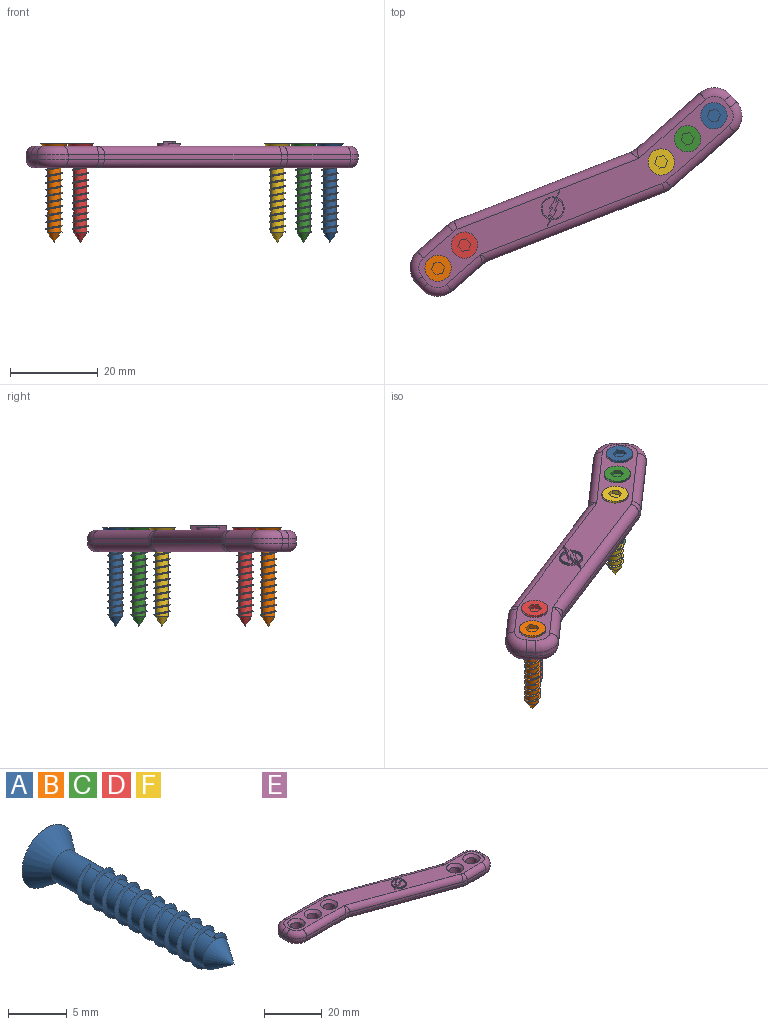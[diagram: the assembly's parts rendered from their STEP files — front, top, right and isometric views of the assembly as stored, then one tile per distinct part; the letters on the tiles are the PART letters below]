
ASSEMBLY  parts=6 mates=5
PART A: 25 faces, bbox 6x22.5x6 mm
  f0: plane 6x6mm, normal (0,1,0), area 22.4mm2, adj f12,f18,f19,f20,f21,f22,f23
  f1: cylinder r=1.5mm len=4.5mm, axis (0,1,0), area 35.3mm2, adj f10,f12,f13,f16
  f2: cylinder r=1.5mm len=3mm, axis (0,1,0), area 11.3mm2, adj f3,f11,f15,f16
  f3: cylinder r=1.5mm len=3mm, axis (0,1,0), area 11.3mm2, adj f2,f4,f15,f16
  f4: cylinder r=1.5mm len=3mm, axis (0,1,0), area 11.3mm2, adj f3,f5,f15,f16
  f5: cylinder r=1.5mm len=3mm, axis (0,1,0), area 11.3mm2, adj f4,f6,f15,f16
  f6: cylinder r=1.5mm len=3mm, axis (0,1,0), area 11.3mm2, adj f5,f7,f15,f16
  f7: cylinder r=1.5mm len=3mm, axis (0,1,0), area 11.3mm2, adj f6,f8,f15,f16
  f8: cylinder r=1.5mm len=3mm, axis (0,1,0), area 11.3mm2, adj f7,f9,f15,f16
  f9: cylinder r=1.5mm len=3mm, axis (0,1,0), area 11.3mm2, adj f8,f10,f15,f16
  f10: cylinder r=1.5mm len=3mm, axis (0,1,0), area 11.3mm2, adj f1,f9,f15,f16
  f11: cylinder r=1.5mm len=3mm, axis (0,1,0), area 7.1mm2, adj f2,f14,f15,f17
  f12: cone r=3mm half-angle=36.9deg, axis (0,1,0), area 35.3mm2, adj f0,f1
  f13: plane 0.37x0.3mm, normal (1,0,0), area 0.1mm2, adj f1,f15,f16
  f14: plane 0.37x0.3mm, normal (-1,0,0), area 0.1mm2, adj f11,f15,f16
  f15: bspline ~15.15x4.32mm, area 42.6mm2, adj f2,f3,f4,f5,f6,f7,f8,f9
  f16: bspline ~15.15x4.32mm, area 42.7mm2, adj f1,f2,f3,f4,f5,f6,f7,f8
  f17: cone r=1.5mm half-angle=34.3deg, axis (0,1,0), area 12.5mm2, adj f11
  f18: plane 1.3x1mm, normal (-0.5,0,-0.87), area 1.5mm2, adj f0,f19,f23,f24
  f19: plane 1.5x1mm, normal (-1,0,0), area 1.5mm2, adj f0,f18,f20,f24
  f20: plane 1.3x1mm, normal (-0.5,0,0.87), area 1.5mm2, adj f0,f19,f21,f24
  f21: plane 1.3x1mm, normal (0.5,0,0.87), area 1.5mm2, adj f0,f20,f22,f24
  f22: plane 1.5x1mm, normal (1,0,0), area 1.5mm2, adj f0,f21,f23,f24
  f23: plane 1.3x1mm, normal (0.5,0,-0.87), area 1.5mm2, adj f0,f18,f22,f24
  f24: plane 3x2.6mm, normal (0,1,0), area 5.8mm2, adj f18,f19,f20,f21,f22,f23
PART B: same geometry as A
PART C: same geometry as A
PART D: same geometry as A
PART E: 81 faces, bbox 83.1x28.2x6 mm
  f0: plane 78.29x23.39mm, normal (0,0,1), area 458.3mm2, adj f23,f24,f25,f26,f27,f28,f29,f30
  f1: plane 78.29x23.39mm, normal (0,0,-1), area 544.8mm2, adj f10,f11,f12,f13,f14,f15,f16,f17
  f2: plane 2x1mm, normal (-1,0,0), area 2mm2, adj f16,f24,f44,f47
  f3: plane 19.12x1mm, normal (0,-1,0), area 19.1mm2, adj f18,f26,f47,f50
  f4: plane 40.63x14.79mm, normal (-0.34,-0.94,0), area 43.2mm2, adj f20,f28,f35,f50
  f5: plane 9.12x1mm, normal (0,-1,0), area 9.1mm2, adj f22,f30,f32,f35
  f6: plane 2x1mm, normal (1,0,0), area 2mm2, adj f21,f29,f32,f38
  f7: plane 9.12x1mm, normal (0,1,0), area 9.1mm2, adj f19,f27,f38,f53
  f8: plane 40.63x14.79mm, normal (0.34,0.94,0), area 43.2mm2, adj f17,f25,f41,f53
  f9: plane 19.12x1mm, normal (0,1,0), area 19.1mm2, adj f15,f23,f41,f44
  f10: cylinder r=2mm len=4mm, axis (0,0,1), area 50.3mm2, adj f1,f56
  f11: cylinder r=2mm len=4mm, axis (0,0,1), area 50.3mm2, adj f1,f59
  f12: cylinder r=2mm len=4mm, axis (0,0,1), area 50.3mm2, adj f1,f57
  f13: cylinder r=2mm len=4mm, axis (0,0,1), area 50.3mm2, adj f1,f58
  f14: cylinder r=2mm len=4mm, axis (0,0,1), area 50.3mm2, adj f1,f55
  f15: cylinder r=2mm len=19.12mm, axis (-1,0,0), area 60.1mm2, adj f1,f9,f42,f45
  f16: cylinder r=2mm len=2mm, axis (0,-1,0), area 6.3mm2, adj f1,f2,f45,f48
  f17: cylinder r=2mm len=42.47mm, axis (-0.94,0.34,0), area 137.2mm2, adj f1,f8,f42,f52
  f18: cylinder r=2mm len=20.35mm, axis (1,0,0), area 61.5mm2, adj f1,f3,f48,f49
  f19: cylinder r=2mm len=10.35mm, axis (-1,0,0), area 30.1mm2, adj f1,f7,f39,f52
  f20: cylinder r=2mm len=42.47mm, axis (0.94,-0.34,0), area 137.2mm2, adj f1,f4,f36,f49
  f21: cylinder r=2mm len=2mm, axis (0,1,0), area 6.3mm2, adj f1,f6,f33,f39
  f22: cylinder r=2mm len=9.12mm, axis (1,0,0), area 28.6mm2, adj f1,f5,f33,f36
  f23: cylinder r=2mm len=19.12mm, axis (1,0,0), area 60.1mm2, adj f0,f9,f40,f43
  f24: cylinder r=2mm len=2mm, axis (0,1,0), area 6.3mm2, adj f0,f2,f43,f46
  f25: cylinder r=2mm len=42.47mm, axis (0.94,-0.34,0), area 137.2mm2, adj f0,f8,f40,f54
  f26: cylinder r=2mm len=20.35mm, axis (-1,0,0), area 61.5mm2, adj f0,f3,f46,f51
  f27: cylinder r=2mm len=10.35mm, axis (1,0,0), area 30.1mm2, adj f0,f7,f37,f54
  f28: cylinder r=2mm len=42.47mm, axis (-0.94,0.34,0), area 137.2mm2, adj f0,f4,f34,f51
  f29: cylinder r=2mm len=2mm, axis (0,-1,0), area 6.3mm2, adj f0,f6,f31,f37
  f30: cylinder r=2mm len=9.12mm, axis (-1,0,0), area 28.6mm2, adj f0,f5,f31,f34
  f31: torus R=3mm, axis (0,0,1), area 21.1mm2, adj f0,f29,f30,f32
  f32: cylinder r=5mm len=5mm, axis (0,0,1), area 7.9mm2, adj f5,f6,f31,f33
  f33: torus R=3mm, axis (0,0,1), area 21.1mm2, adj f1,f21,f22,f32
  f34: torus R=3mm, axis (0,0,1), area 4.7mm2, adj f0,f28,f30,f35
  f35: cylinder r=5mm len=1.71mm, axis (0,0,1), area 1.7mm2, adj f4,f5,f34,f36
  f36: torus R=3mm, axis (0,0,1), area 4.7mm2, adj f1,f20,f22,f35
  f37: torus R=3mm, axis (0,0,1), area 21.1mm2, adj f0,f27,f29,f38
  f38: cylinder r=5mm len=5mm, axis (0,0,-1), area 7.9mm2, adj f6,f7,f37,f39
  f39: torus R=3mm, axis (0,0,1), area 21.1mm2, adj f1,f19,f21,f38
  f40: torus R=3mm, axis (0,0,1), area 4.7mm2, adj f0,f23,f25,f41
  f41: cylinder r=5mm len=1.71mm, axis (0,0,-1), area 1.7mm2, adj f8,f9,f40,f42
  f42: torus R=3mm, axis (0,0,1), area 4.7mm2, adj f1,f15,f17,f41
  f43: torus R=3mm, axis (0,0,1), area 21.1mm2, adj f0,f23,f24,f44
  f44: cylinder r=5mm len=5mm, axis (0,0,1), area 7.9mm2, adj f2,f9,f43,f45
  f45: torus R=3mm, axis (0,0,1), area 21.1mm2, adj f1,f15,f16,f44
  f46: torus R=3mm, axis (0,0,1), area 21.1mm2, adj f0,f24,f26,f47
  f47: cylinder r=5mm len=5mm, axis (0,0,-1), area 7.9mm2, adj f2,f3,f46,f48
  f48: torus R=3mm, axis (0,0,1), area 21.1mm2, adj f1,f16,f18,f47
  f49: bspline ~2.3x2.26mm, area 3.5mm2, adj f18,f20,f50
  f50: cylinder r=5mm len=1.71mm, axis (0,0,-1), area 1.7mm2, adj f3,f4,f49,f51
  f51: bspline ~2.3x2.26mm, area 3.5mm2, adj f26,f28,f50
  f52: bspline ~2.3x2.26mm, area 3.5mm2, adj f17,f19,f53
  f53: cylinder r=5mm len=1.71mm, axis (0,0,1), area 1.7mm2, adj f7,f8,f52,f54
  f54: bspline ~2.3x2.26mm, area 3.5mm2, adj f25,f27,f53
  f55: cone r=2mm half-angle=45deg, axis (0,0,1), area 22.2mm2, adj f0,f14
  f56: cone r=2mm half-angle=45deg, axis (0,0,1), area 22.2mm2, adj f0,f10
  f57: cone r=2mm half-angle=45deg, axis (0,0,1), area 22.2mm2, adj f0,f12
  f58: cone r=2mm half-angle=45deg, axis (0,0,1), area 22.2mm2, adj f0,f13
  f59: cone r=2mm half-angle=45deg, axis (0,0,1), area 22.2mm2, adj f0,f11
  f60: plane 4.48x1.48mm, normal (0.31,-0.95,0), area 4.7mm2, adj f0,f61,f69,f80
  f61: plane 1x0.75mm, normal (0.34,0.94,0), area 0.8mm2, adj f0,f60,f62,f80
  f62: plane 2.1x1mm, normal (0.38,-0.93,0), area 2.3mm2, adj f0,f61,f63,f80
  f63: plane 1x0.75mm, normal (0.34,0.94,0), area 0.8mm2, adj f0,f62,f64,f80
  f64: plane 2.52x1.42mm, normal (0.49,-0.87,0), area 2.9mm2, adj f0,f63,f65,f80
  f65: plane 4.27x1.5mm, normal (-0.33,0.94,0), area 4.5mm2, adj f0,f64,f66,f80
  f66: plane 1x0.67mm, normal (-0.34,-0.94,0), area 0.7mm2, adj f0,f65,f67,f80
  f67: plane 2.34x1mm, normal (-0.38,0.93,0), area 2.5mm2, adj f0,f66,f68,f80
  f68: plane 1x0.74mm, normal (-0.34,-0.94,0), area 0.8mm2, adj f0,f67,f69,f80
  f69: plane 2.41x1.34mm, normal (-0.49,0.87,0), area 2.8mm2, adj f0,f60,f68,f80
  f70: plane 0.5x0.19mm, normal (-0.38,0.93,0), area 0.1mm2, adj f0,f71,f73,f74
  f71: cylinder r=2.63mm len=4.76mm, axis (0,0,-1), area 4.1mm2, adj f0,f70,f72,f74
  f72: plane 0.5x0.15mm, normal (-0.73,0.68,0), area 0.1mm2, adj f0,f71,f73,f74
  f73: cylinder r=2.43mm len=4.37mm, axis (0,0,-1), area 3.7mm2, adj f0,f70,f72,f74
  f74: plane 4.76x4.07mm, normal (0,0,1), area 1.6mm2, adj f70,f71,f72,f73
  f75: plane 0.5x0.15mm, normal (0.73,-0.68,0), area 0.1mm2, adj f0,f76,f78,f79
  f76: cylinder r=2.63mm len=4.43mm, axis (0,0,-1), area 3.6mm2, adj f0,f75,f77,f79
  f77: plane 0.5x0.19mm, normal (0.38,-0.93,0), area 0.1mm2, adj f0,f76,f78,f79
  f78: cylinder r=2.43mm len=4.09mm, axis (0,0,-1), area 3.3mm2, adj f0,f75,f77,f79
  f79: plane 4.43x3.62mm, normal (0,0,1), area 1.4mm2, adj f75,f76,f77,f78
  f80: plane 7.6x4.3mm, normal (0,0,1), area 5.1mm2, adj f60,f61,f62,f63,f64,f65,f66,f67
PART F: same geometry as A
PLACE A rot(axis=(0.5,0.61,0.61),126.7deg) t=(-17.54,54.16,27.83)mm
PLACE B rot(axis=(0.5,0.61,0.61),126.7deg) t=(-80.5,19.34,27.83)mm
PLACE C rot(axis=(0.5,0.61,0.61),126.7deg) t=(-23.55,48.88,27.83)mm
PLACE D rot(axis=(0.5,0.61,0.61),126.7deg) t=(-74.49,24.62,27.83)mm
PLACE E rot(axis=(0,0,-1),138.7deg) t=(-9.07,53.62,22.33)mm
PLACE F rot(axis=(0.5,0.61,0.61),126.7deg) t=(-29.56,43.6,27.83)mm
MATE cylindrical D.f1 <-> E.f10  axis (0,0,1) through (-74.49,24.62,25.83)mm
MATE cylindrical B.f1 <-> E.f14  axis (0,0,1) through (-80.5,19.34,25.83)mm
MATE cylindrical C.f1 <-> E.f13  axis (0,0,1) through (-23.55,48.88,25.83)mm
MATE cylindrical F.f1 <-> E.f12  axis (0,0,1) through (-29.56,43.6,25.83)mm
MATE cylindrical A.f1 <-> E.f11  axis (0,0,1) through (-17.54,54.16,25.83)mm
